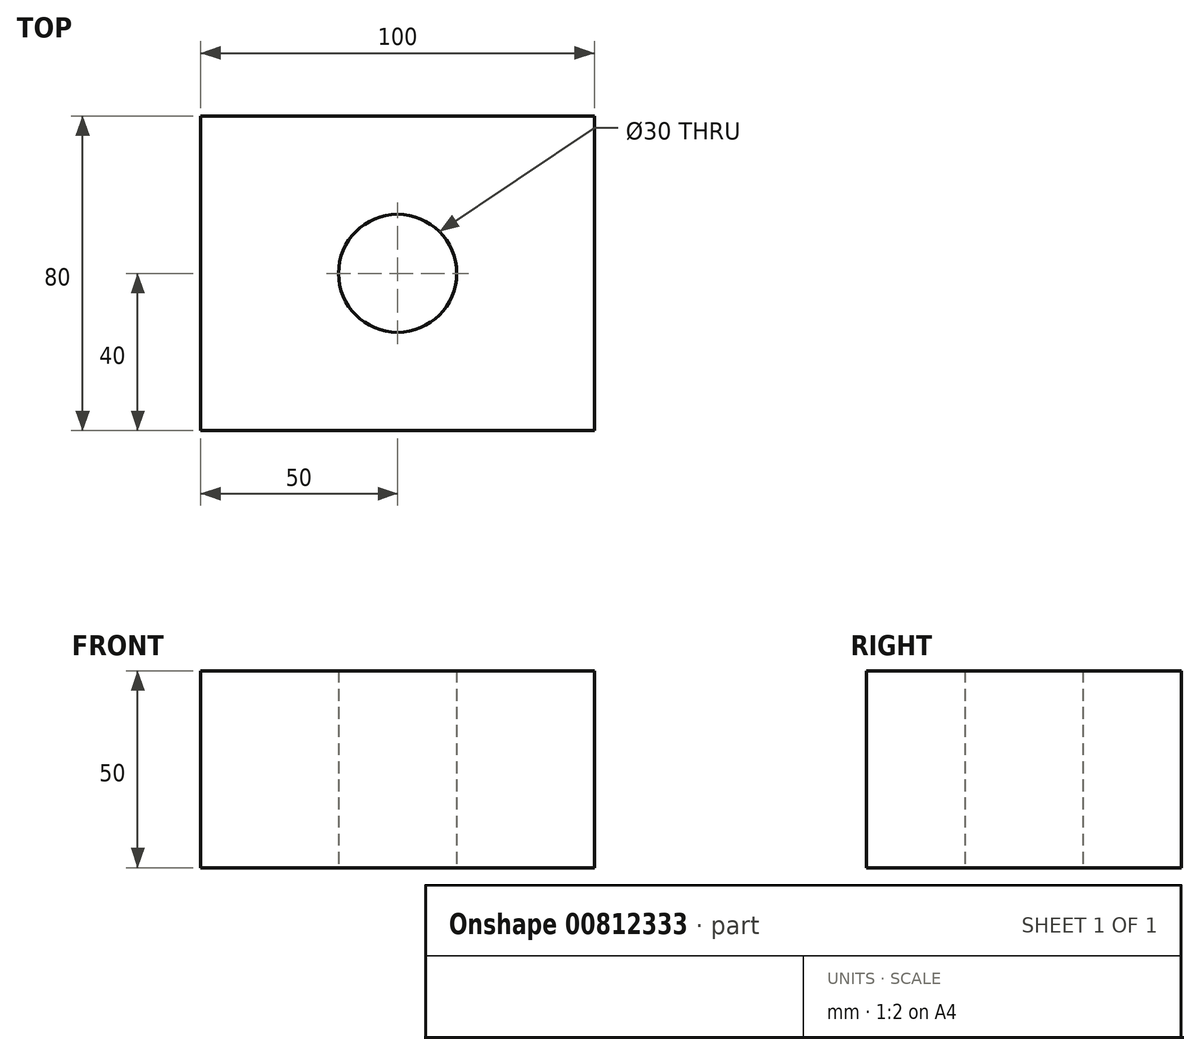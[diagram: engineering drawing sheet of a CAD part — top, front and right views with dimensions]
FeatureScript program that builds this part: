
annotation { "Feature Type Name" : "Feature", "Feature Type Description" : "" }
export const myFeature = defineFeature(function(context is Context, id is Id, definition is map)
    precondition{}
    {
        {
            var Q0;
            Q0=qCreatedBy(makeId("Top.planeOp"),FACE);
            var sketch = newSketch(context, id + "F0", { "sketchPlane" : qUnion([Q0])});
            skLineSegment(sketch, "E0.bottom", {"start": v(-50, 40) * mm, "end": v(50, 40) * mm});
            skLineSegment(sketch, "E0.top", {"start": v(-50, -40) * mm, "end": v(50, -40) * mm});
            skLineSegment(sketch, "E0.left", {"start": v(-50, 40) * mm, "end": v(-50, -40) * mm});
            skLineSegment(sketch, "E0.right", {"start": v(50, 40) * mm, "end": v(50, -40) * mm});
            skCircle(sketch, "E1", {"center": v(0, 0) * mm, "radius": 15 * mm});
            skSolve(sketch);
        }
        {
            var Q0;
            Q0=makeQuery(id+"F0.imprint","IMPRINT",FACE,{"disambiguationData":[TD([[makeQuery(id+"F0.imprint","IMPRINT",EDGE,{"derivedFrom":sQuery(id+"F0.wireOp",EDGE,"E0.bottom")}),-1.0]])]});
            extrude(context, id + "F1", {"entities" : qUnion([Q0]), "depth" : 50 * mm, "offsetDistance" : 25 * mm});
        }
    });
